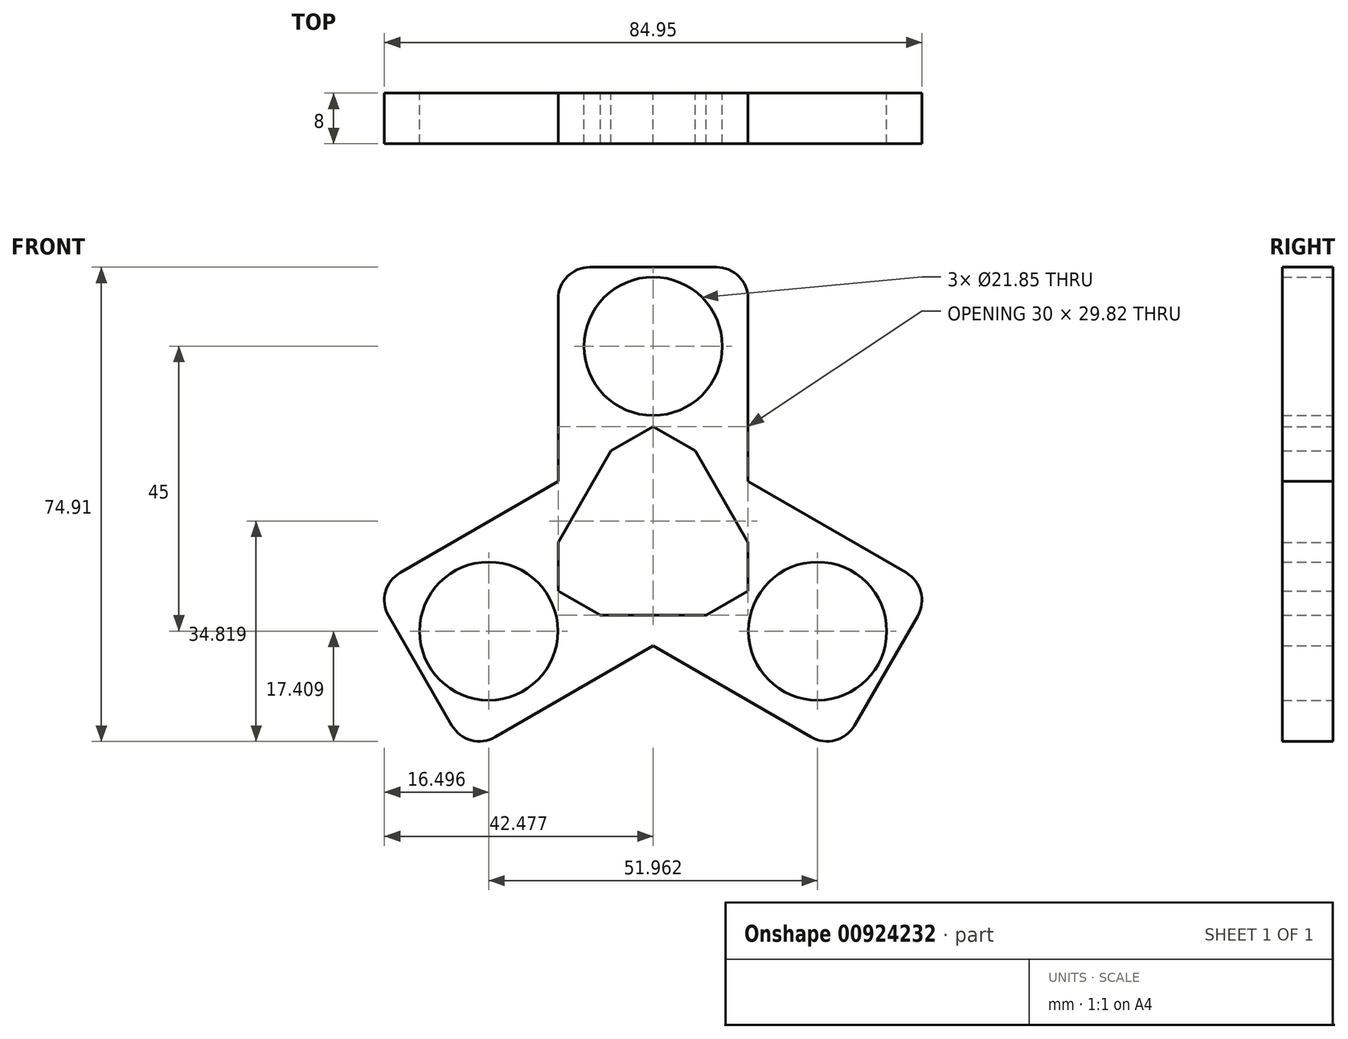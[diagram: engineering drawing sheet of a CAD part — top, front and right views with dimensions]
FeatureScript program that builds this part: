
annotation { "Feature Type Name" : "Feature", "Feature Type Description" : "" }
export const myFeature = defineFeature(function(context is Context, id is Id, definition is map)
    precondition{}
    {
        {
            var Q0;
            Q0=qCreatedBy(makeId("Front.planeOp"),FACE);
            var sketch = newSketch(context, id + "F0", { "sketchPlane" : qUnion([Q0])});
            skCircle(sketch, "E0", {"center": v(212.16, 282.63) * mm, "radius": 10.93 * mm});
            skCircle(sketch, "E1", {"center": v(212.16, 312.63) * mm, "radius": 10.93 * mm});
            skLineSegment(sketch, "E2", {"start": v(212.16, 312.63) * mm, "end": v(212.16, 282.63) * mm, "construction": true});
            skPoint(sketch, "E3", {"position": v(212.16, 297.63) * mm});
            skLineSegment(sketch, "E4.bottom", {"start": v(222.16, 325.13) * mm, "end": v(202.16, 325.13) * mm});
            skLineSegment(sketch, "E4.top", {"start": v(227.16, 270.13) * mm, "end": v(197.16, 270.13) * mm});
            skLineSegment(sketch, "E4.left", {"start": v(227.16, 320.13) * mm, "end": v(227.16, 270.13) * mm});
            skLineSegment(sketch, "E4.right", {"start": v(197.16, 320.13) * mm, "end": v(197.16, 270.13) * mm});
            skPoint(sketch, "E5.visualSharp", {"position": v(227.16, 325.13) * mm});
            skArc(sketch, "E5.filletArc", {"start": v(227.16, 320.13) * mm, "mid": v(225.7, 323.66) * mm, "end": v(222.16, 325.13) * mm});
            skPoint(sketch, "E6.visualSharp", {"position": v(197.16, 325.13) * mm});
            skArc(sketch, "E6.filletArc", {"start": v(202.16, 325.13) * mm, "mid": v(198.62, 323.66) * mm, "end": v(197.16, 320.13) * mm});
            skLineSegment(sketch, "E7.1.0", {"start": v(215.48, 301.87) * mm, "end": v(230.48, 275.89) * mm});
            skPoint(sketch, "E7.1.1", {"position": v(182.85, 248.39) * mm});
            skLineSegment(sketch, "E7.1.2", {"start": v(187.18, 250.89) * mm, "end": v(230.48, 275.89) * mm});
            skLineSegment(sketch, "E7.1.3", {"start": v(170.35, 270.04) * mm, "end": v(180.35, 252.72) * mm});
            skCircle(sketch, "E7.1.4", {"center": v(186.18, 267.63) * mm, "radius": 10.93 * mm});
            skPoint(sketch, "E7.1.5", {"position": v(167.85, 274.37) * mm});
            skLineSegment(sketch, "E7.1.7", {"start": v(172.18, 276.87) * mm, "end": v(215.48, 301.87) * mm});
            skPoint(sketch, "E7.1.8", {"position": v(199.17, 275.13) * mm});
            skLineSegment(sketch, "E7.1.9", {"start": v(186.18, 267.63) * mm, "end": v(212.16, 282.63) * mm, "construction": true});
            skPoint(sketch, "E7.1.10", {"position": v(199.17, 275.13) * mm});
            skArc(sketch, "E7.1.11", {"start": v(180.35, 252.72) * mm, "mid": v(183.39, 250.39) * mm, "end": v(187.18, 250.89) * mm});
            skArc(sketch, "E7.1.12", {"start": v(172.18, 276.87) * mm, "mid": v(169.85, 273.83) * mm, "end": v(170.35, 270.04) * mm});
            skLineSegment(sketch, "E7.2.0", {"start": v(193.83, 275.89) * mm, "end": v(208.83, 301.87) * mm});
            skPoint(sketch, "E7.2.1", {"position": v(256.46, 274.37) * mm});
            skLineSegment(sketch, "E7.2.2", {"start": v(252.13, 276.87) * mm, "end": v(208.83, 301.87) * mm});
            skLineSegment(sketch, "E7.2.3", {"start": v(243.96, 252.72) * mm, "end": v(253.96, 270.04) * mm});
            skCircle(sketch, "E7.2.4", {"center": v(238.14, 267.63) * mm, "radius": 10.93 * mm});
            skPoint(sketch, "E7.2.5", {"position": v(241.46, 248.39) * mm});
            skLineSegment(sketch, "E7.2.7", {"start": v(237.13, 250.89) * mm, "end": v(193.83, 275.89) * mm});
            skPoint(sketch, "E7.2.8", {"position": v(225.15, 275.13) * mm});
            skLineSegment(sketch, "E7.2.9", {"start": v(238.14, 267.63) * mm, "end": v(212.16, 282.63) * mm, "construction": true});
            skPoint(sketch, "E7.2.10", {"position": v(225.15, 275.13) * mm});
            skArc(sketch, "E7.2.11", {"start": v(253.96, 270.04) * mm, "mid": v(254.46, 273.83) * mm, "end": v(252.13, 276.87) * mm});
            skArc(sketch, "E7.2.12", {"start": v(237.13, 250.89) * mm, "mid": v(240.93, 250.39) * mm, "end": v(243.96, 252.72) * mm});
            skSolve(sketch);
        }
        {
            var Q0;
            Q0 = qSketchRegion(id + "F0", true);
            var Q1;
            {var subQ0=sQuery(id+"F0.wireOp",EDGE,"E7.2.0");var subQ1=sQuery(id+"F0.wireOp",EDGE,"E7.1.7");var subQ2=makeQuery(id+"F0.imprint","INTERSECT",VERTEX,{"derivedFrom":[subQ1,subQ0]});Q1=makeQuery(id+"F0.imprint","IMPRINT",FACE,{"disambiguationData":[TD([[makeQuery(id+"F0.imprint","IMPRINT",EDGE,{"disambiguationData":[TD([[subQ2,-1.0]])],"derivedFrom":subQ1}),1.0]])]});}
            var Q2;
            {var subQ0=sQuery(id+"F0.wireOp",EDGE,"E7.1.7");var subQ1=sQuery(id+"F0.wireOp",EDGE,"E7.1.0");var subQ2=makeQuery(id+"F0.imprint","INTERSECT",VERTEX,{"derivedFrom":[subQ1,subQ0]});Q2=makeQuery(id+"F0.imprint","IMPRINT",FACE,{"disambiguationData":[TD([[makeQuery(id+"F0.imprint","IMPRINT",EDGE,{"disambiguationData":[TD([[subQ2,-1.0]])],"derivedFrom":subQ1}),-1.0]])]});}
            var Q3;
            Q3=makeQuery(id+"F0.imprint","IMPRINT",FACE,{"disambiguationData":[TD([[makeQuery(id+"F0.imprint","IMPRINT",EDGE,{"derivedFrom":sQuery(id+"F0.wireOp",EDGE,"E0")}),-1.0]])]});
            var Q4;
            {var subQ0=sQuery(id+"F0.wireOp",EDGE,"E7.2.0");var subQ1=sQuery(id+"F0.wireOp",EDGE,"E4.right");var subQ2=makeQuery(id+"F0.imprint","INTERSECT",VERTEX,{"derivedFrom":[subQ1,subQ0]});Q4=makeQuery(id+"F0.imprint","IMPRINT",FACE,{"disambiguationData":[TD([[makeQuery(id+"F0.imprint","IMPRINT",EDGE,{"disambiguationData":[TD([[subQ2,-1.0]])],"derivedFrom":subQ1}),-1.0]])]});}
            var Q5;
            {var subQ0=sQuery(id+"F0.wireOp",EDGE,"E4.right");var subQ1=sQuery(id+"F0.wireOp",EDGE,"E4.top");var subQ2=makeQuery(id+"F0.imprint","INTERSECT",VERTEX,{"derivedFrom":[subQ1,subQ0]});Q5=makeQuery(id+"F0.imprint","IMPRINT",FACE,{"disambiguationData":[TD([[makeQuery(id+"F0.imprint","IMPRINT",EDGE,{"disambiguationData":[TD([[subQ2,1.0]])],"derivedFrom":subQ1}),-1.0]])]});}
            var Q6;
            {var subQ0=sQuery(id+"F0.wireOp",EDGE,"E4.left");var subQ1=sQuery(id+"F0.wireOp",EDGE,"E4.top");var subQ2=makeQuery(id+"F0.imprint","INTERSECT",VERTEX,{"derivedFrom":[subQ1,subQ0]});Q6=makeQuery(id+"F0.imprint","IMPRINT",FACE,{"disambiguationData":[TD([[makeQuery(id+"F0.imprint","IMPRINT",EDGE,{"disambiguationData":[TD([[subQ2,-1.0]])],"derivedFrom":subQ1}),-1.0]])]});}
            var Q7;
            {var subQ0=sQuery(id+"F0.wireOp",EDGE,"E7.1.0");var subQ1=sQuery(id+"F0.wireOp",EDGE,"E4.left");var subQ2=makeQuery(id+"F0.imprint","INTERSECT",VERTEX,{"derivedFrom":[subQ1,subQ0]});Q7=makeQuery(id+"F0.imprint","IMPRINT",FACE,{"disambiguationData":[TD([[makeQuery(id+"F0.imprint","IMPRINT",EDGE,{"disambiguationData":[TD([[subQ2,-1.0]])],"derivedFrom":subQ1}),1.0]])]});}
            extrude(context, id + "F1", {"entities" : qUnion([Q0, Q1, Q2, Q3, Q4, Q5, Q6, Q7]), "depth" : 8 * mm, "offsetDistance" : 25 * mm});
        }
    });
